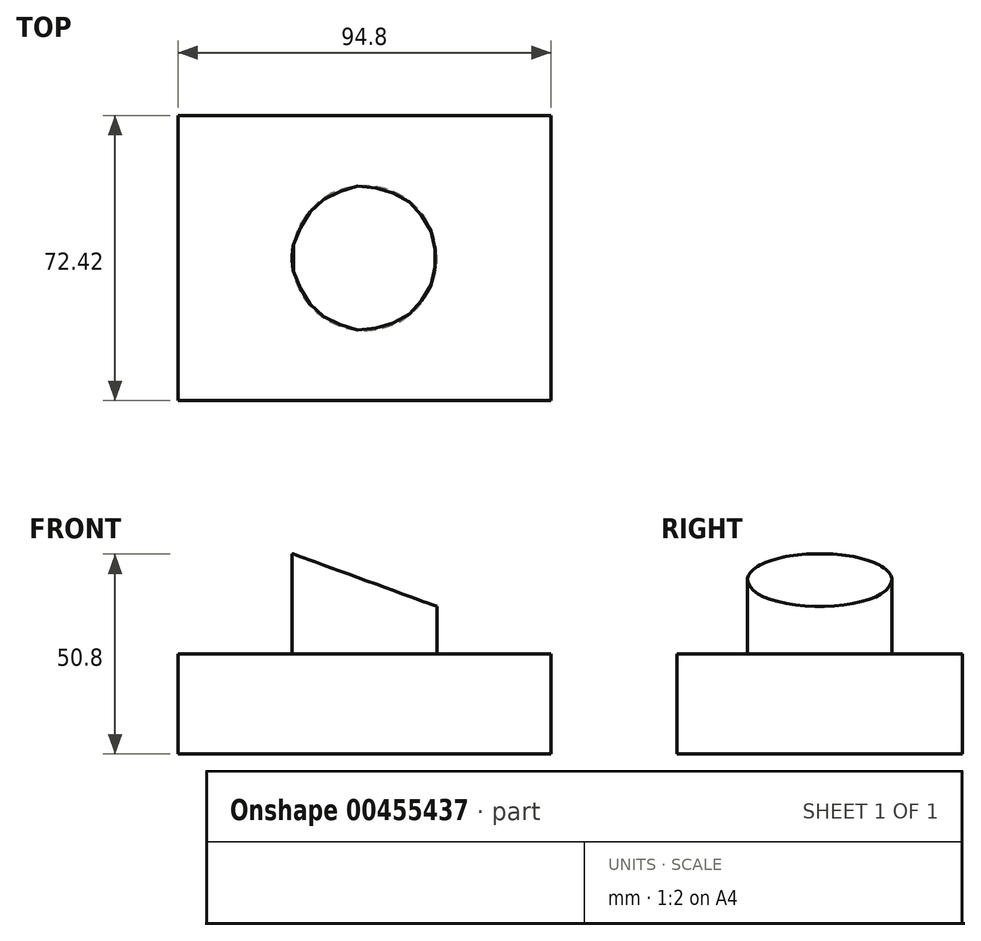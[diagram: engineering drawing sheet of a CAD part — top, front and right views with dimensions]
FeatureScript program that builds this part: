
annotation { "Feature Type Name" : "Feature", "Feature Type Description" : "" }
export const myFeature = defineFeature(function(context is Context, id is Id, definition is map)
    precondition{}
    {
        {
            var Q0;
            Q0=qCreatedBy(makeId("Top.planeOp"),FACE);
            var sketch = newSketch(context, id + "F0", { "sketchPlane" : qUnion([Q0])});
            skLineSegment(sketch, "E0.bottom", {"start": v(47.4, -36.21) * mm, "end": v(-47.4, -36.21) * mm});
            skLineSegment(sketch, "E0.top", {"start": v(47.4, 36.21) * mm, "end": v(-47.4, 36.21) * mm});
            skLineSegment(sketch, "E0.left", {"start": v(47.4, -36.21) * mm, "end": v(47.4, 36.21) * mm});
            skLineSegment(sketch, "E0.right", {"start": v(-47.4, -36.21) * mm, "end": v(-47.4, 36.21) * mm});
            skPoint(sketch, "E0.middle", {"position": v(0, 0) * mm});
            skSolve(sketch);
        }
        {
            var Q0;
            Q0 = qSketchRegion(id + "F0", true);
            extrude(context, id + "F1", {"entities" : qUnion([Q0]), "depth" : 25.4 * mm});
        }
        {
            var Q0;
            Q0=makeQuery(id+"F1.opExtrude","CAP_FACE",FACE,{"disambiguationData":[OSD([sQuery(id+"F0.wireOp",EDGE,"E0.bottom"),sQuery(id+"F0.wireOp",EDGE,"E0.top"),sQuery(id+"F0.wireOp",EDGE,"E0.left"),sQuery(id+"F0.wireOp",EDGE,"E0.right")])],"isStart":false});
            var sketch = newSketch(context, id + "F2", { "sketchPlane" : qUnion([Q0])});
            skCircle(sketch, "E1", {"center": v(0, 0) * mm, "radius": 18.4 * mm});
            skSolve(sketch);
        }
        {
            var Q0;
            Q0 = qSketchRegion(id + "F2", true);
            extrude(context, id + "F3", {"entities" : qUnion([Q0]), "operationType" : NewBodyOperationType.ADD, "depth" : 25.4 * mm});
        }
        {
            var Q0;
            Q0=qCreatedBy(makeId("Front.planeOp"),FACE);
            var sketch = newSketch(context, id + "F4", { "sketchPlane" : qUnion([Q0])});
            skLineSegment(sketch, "E2", {"start": v(-19.15, 51.2) * mm, "end": v(19.67, 37) * mm});
            skLineSegment(sketch, "E3", {"start": v(19.67, 37) * mm, "end": v(19.67, 52.77) * mm});
            skLineSegment(sketch, "E4", {"start": v(19.67, 52.77) * mm, "end": v(-19.15, 51.2) * mm});
            skSolve(sketch);
        }
        {
            var Q0;
            Q0 = qSketchRegion(id + "F4", true);
            extrude(context, id + "F5", {"entities" : qUnion([Q0]), "operationType" : NewBodyOperationType.REMOVE, "endBound" : BoundingType.THROUGH_ALL, "oppositeDirection" : true, "depth" : 25.4 * mm, "hasSecondDirection" : true, "secondDirectionBound" : SecondDirectionBoundingType.THROUGH_ALL, "secondDirectionOppositeDirection" : false, "secondDirectionDepth" : 25.4 * mm});
        }
    });
